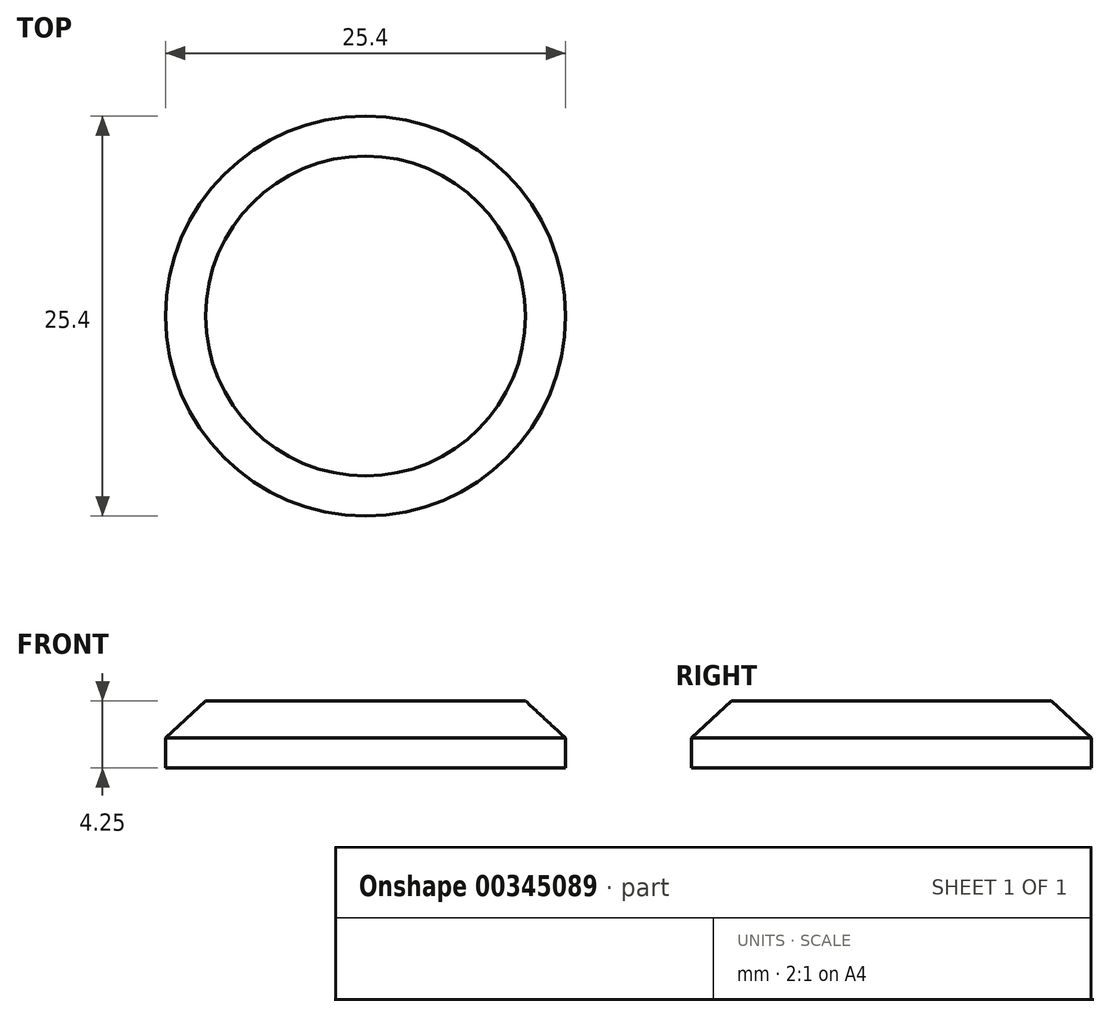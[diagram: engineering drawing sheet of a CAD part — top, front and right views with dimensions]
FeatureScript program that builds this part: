
annotation { "Feature Type Name" : "Feature", "Feature Type Description" : "" }
export const myFeature = defineFeature(function(context is Context, id is Id, definition is map)
    precondition{}
    {
        {
            var Q0;
            Q0=qCreatedBy(makeId("Front.planeOp"),FACE);
            var sketch = newSketch(context, id + "F0", { "sketchPlane" : qUnion([Q0])});
            skLineSegment(sketch, "E0", {"start": v(0, 0) * mm, "end": v(12.7, 0) * mm});
            skLineSegment(sketch, "E1", {"start": v(12.7, 0) * mm, "end": v(12.7, 1.89) * mm});
            skLineSegment(sketch, "E2", {"start": v(12.7, 1.89) * mm, "end": v(10.16, 4.25) * mm});
            skPoint(sketch, "E3.2.internal.orphan", {"position": v(10.16, 20.3) * mm});
            skPoint(sketch, "E3.5.internal.orphan", {"position": v(10.16, 28.56) * mm});
            skLineSegment(sketch, "E4", {"start": v(10.16, 4.25) * mm, "end": v(0, 4.25) * mm});
            skLineSegment(sketch, "E5", {"start": v(0, 4.25) * mm, "end": v(0, 0) * mm});
            skSolve(sketch);
        }
        {
            var Q0;
            Q0 = qSketchRegion(id + "F0", true);
            var Q1;
            Q1=sQuery(id+"F0.wireOp",EDGE,"E5");
            revolve(context, id + "F1", {"entities" : qUnion([Q0]), "axis" : qUnion([Q1]), "revolveType" : RevolveType.FULL});
        }
    });
